# Revit family: WCPan-RimEx-WallHung-50cm-Vitra_SentoSeries_7747
name_source: partatom
category: Plumbing Fixtures
revit_build: Autodesk Revit 2017 (Build: 20160225_1515(x64)
units: mm (PartAtom-declared; Revit-internal decimal feet)

## family parameters
Cut with Voids When Loaded = No
Host = Face
OmniClass Number = 23.45.05.21.11
OmniClass Title = Water Closets
Part Type = Normal
Room Calculation Point = No
Round Connector Dimension = Use Diameter
Shared = Yes

## types (4) — shared parameters
BIMobject category = Sanitary - Toilets
Brand = VitrA
CW Connection = Yes
Color = White
Default Elevation = 410 mm  [stored 1.34514 ft]
Design country = Turkey
HW Connection = No
IFC Classification = Sanitary Terminal
Main Material = Ceramic
Manufacturer = VitrA
Manufacturer name = VitrA
Masterformat 2014 Code = 22 45 26
Masterformat 2014 Description = Sanitary Facilities
Mounting type = Wall-Hung
NBS Referans Code = 35-65-90
NBS Referans Description = Toilet Systems
Nominal Depth (mm) = 495 mm  [stored 1.62402 ft]
Nominal Height (mm) = 345 mm  [stored 1.13189 ft]
Nominal Width (mm) = 360 mm  [stored 1.1811 ft]
OmniClass Code = 23-31 19 00
OmniClass Description = Toilets
Primary Material = White
Product certification = https://www.vitraglobal.com
Product family = Sento
Product group = Wall Mounted WC
UNSPSC Code = 301815
UNSPSC Description = Sanitary Ware
URL = https://www.vitraglobal.com
Uniclass 1.4 Code = L7216
Uniclass 1.4 Description = Toilets
Uniclass 2.0 Code = SS-35-65-90
Uniclass 2.0 Description = Toilet Systems
Uniclass 2015 Code = Pr_40_20_93
Uniclass 2015 Name = Urinal and WC fittings
Uniformat II Code = D2010
Uniformat II Description = Sanitary Facilities
Vent Connection = No
Warranty Period (Year) = 10 Years
Waste Connection = Yes
Weight Net (kg) = 25.9
Youtube = https://www.youtube.com

## per-type parameters (varying)
| type | Article No. (default) | Description | Model | Product SKU | Product data url | Product url | Technical description | With Bidet Function |
| WCPan-RimEx-WallHung-50cm-White-Vitra_Sento_7747B003-0075 | 7747B003-0075 | VitrA Sento Rim-Ex - 50cm -  WallHung - Wc Pan | 7747B003-0075 | 7747B003-0075 | https://www.bimobject.com | https://www.vitraglobal.com | https://www.vitraglobal.com | No |
| WCPan-RimEx-WallHung-50cm-VitraClean-White-Vitra_Sento_7747B403-0075 | 7747B403-0075 | VitrA Sento Rim-Ex - VitrA Clean - 50cm -  WallHung - Wc Pan | 7747B403-0075 | 7747B403-0075 | https://www.vitra-bad.de |  | https://cdn.vitra.com.tr | No |
| WCPan-RimEx-WallHung-50cm-WithBidetFunction-White-Vitra_Sento_7747B003-0559 | 7747B003-0559 | VitrA Sento Rim-Ex -With Bidet Function- 50cm -  WallHung - Wc Pan | 7747B003-0559 | 7747B003-0559 | https://www.vitra-bad.de |  | https://cdn.vitra.com.tr | Yes |
| WCPan-RimEx-WallHung-50cm-VitraClean-WithBidetFunction-White-Vitra_Sento_7747B403-0559 | 7747B403-0559 | VitrA Sento Rim-Ex - VitrA Clean -With Bidet Function- 50cm -  WallHung - Wc Pan | 7747B403-0559 | 7747B403-0559 | https://www.vitra-bad.de |  | https://cdn.vitra.com.tr | Yes |

note: [stored X ft] marks values corroborated as IEEE doubles in the binary element streams (Revit-internal decimal feet)

## geometry (parser evidence)
native form markers: Sweep x2
no freeform markers — native parametric forms only
